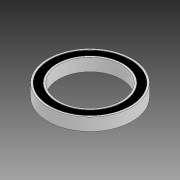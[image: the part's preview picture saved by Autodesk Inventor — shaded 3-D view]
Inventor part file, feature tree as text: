
AUTODESK INVENTOR PART (.ipt)
format: ipt  version: 2020 (Build 240168000, 168)  size: 124,416 bytes
history: native  units: mm
features: revolve x1, sketch x1
ambient origin geometry x8: Origin, YZ Plane, XZ Plane, XY Plane, X Axis, Y Axis, Z Axis, Center Point
bodies: Solid1 (feature_tree)
feature tree (2):
  revolve  "Revolution1"  [1 undecoded]
  sketch  "Sketch1"  dims[d0=17.5mm d2=7.0mm d5=23.5mm d6=0.2mm d7=1.0mm d8=90.0deg]
note: 1 required parameter value undecoded (feature->parameter linkage not recoverable at this tier; creation-order binding heuristic only, values carry confidence <= 0.55)
